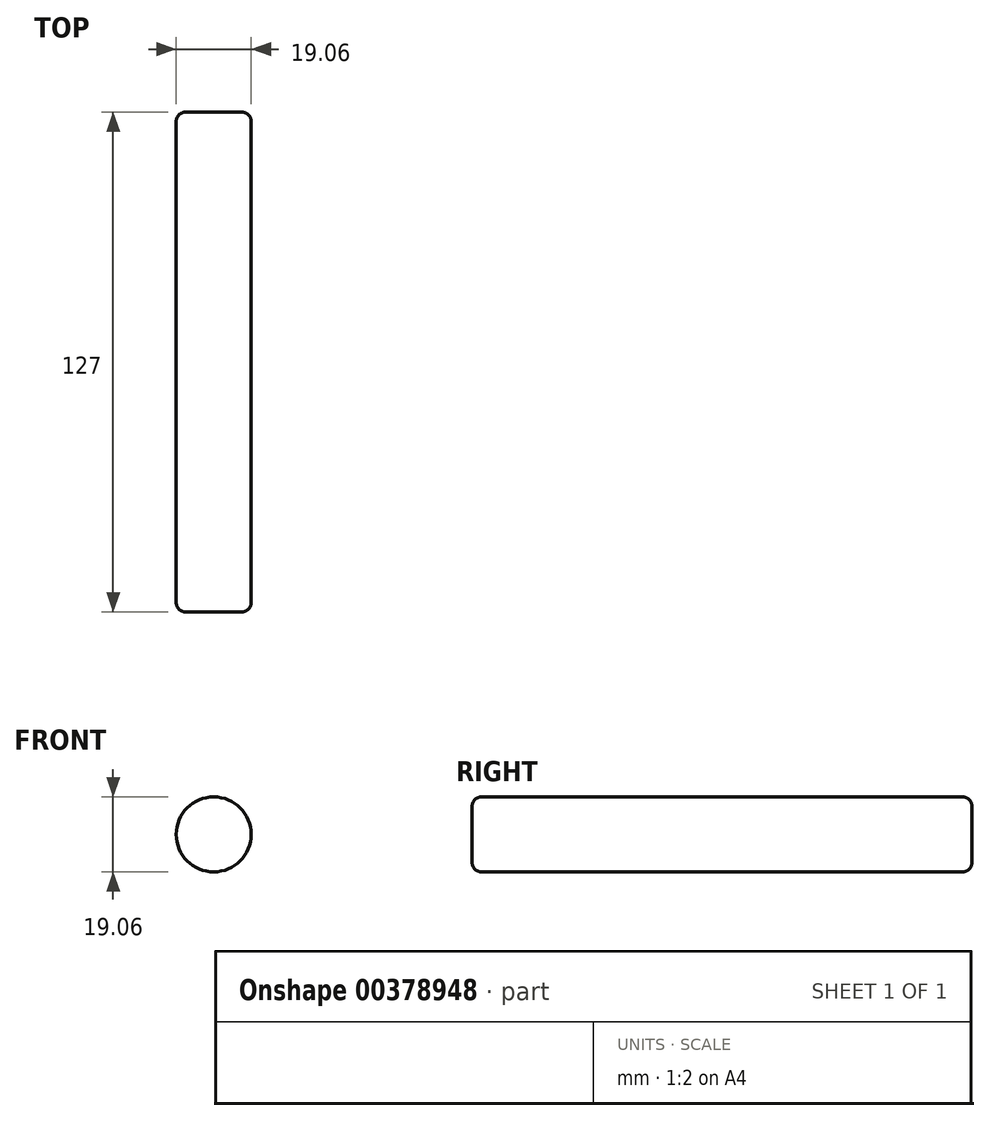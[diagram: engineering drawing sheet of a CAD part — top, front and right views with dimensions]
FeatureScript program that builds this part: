
annotation { "Feature Type Name" : "Feature", "Feature Type Description" : "" }
export const myFeature = defineFeature(function(context is Context, id is Id, definition is map)
    precondition{}
    {
        {
            var Q0;
            Q0=qCreatedBy(makeId("Front.planeOp"),FACE);
            var sketch = newSketch(context, id + "F0", { "sketchPlane" : qUnion([Q0])});
            skCircle(sketch, "E0", {"center": v(0, 0) * mm, "radius": 9.53 * mm});
            skSolve(sketch);
        }
        {
            var Q0;
            Q0=makeQuery(id+"F0.imprint","IMPRINT",FACE,{"disambiguationData":[TD([[makeQuery(id+"F0.imprint","IMPRINT",EDGE,{"derivedFrom":sQuery(id+"F0.wireOp",EDGE,"E0")}),1.0]])]});
            extrude(context, id + "F1", {"entities" : qUnion([Q0]), "endBound" : BoundingType.SYMMETRIC, "depth" : 127 * mm});
        }
        {
            var Q0;
            Q0=makeQuery(id+"F1.opExtrude","CAP_FACE",FACE,{"disambiguationData":[OSD([sQuery(id+"F0.wireOp",EDGE,"E0")])],"isStart":false});
            fillet(context, id + "F2", {"entities" : qUnion([Q0]), "radius" : 2.41 * mm, "tangentPropagation" : true, "allowEdgeOverflow" : false});
        }
        {
            var Q0;
            Q0=makeQuery(id+"F1.opExtrude","CAP_EDGE",EDGE,{"disambiguationData":[OSD([sQuery(id+"F0.wireOp",EDGE,"E0")])],"isStart":true});
            fillet(context, id + "F3", {"entities" : qUnion([Q0]), "radius" : 2.41 * mm, "tangentPropagation" : true, "allowEdgeOverflow" : false});
        }
    });
